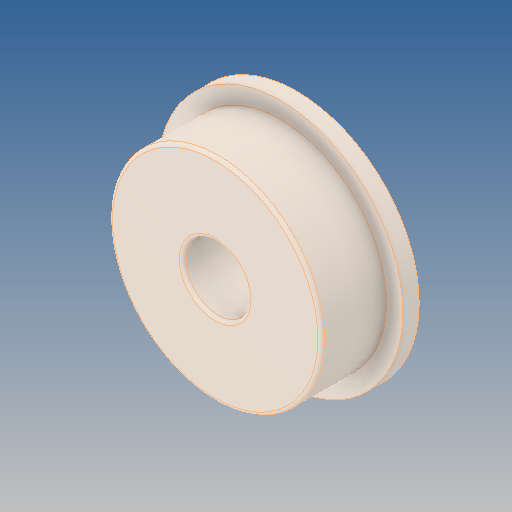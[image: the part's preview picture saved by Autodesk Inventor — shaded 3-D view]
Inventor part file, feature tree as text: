
AUTODESK INVENTOR PART (.ipt)
format: ipt  version: 2019 (Build 230136000, 136)  size: 140,288 bytes
history: native  units: mm
features: fillet x1
ambient origin geometry x8: Origin, YZ Plane, XZ Plane, XY Plane, X Axis, Y Axis, Z Axis, Center Point
bodies: Solid1 (feature_tree)
feature tree (1):
  fillet  "Fillet1"  [1 undecoded]
note: 1 required parameter value undecoded (feature->parameter linkage not recoverable at this tier; creation-order binding heuristic only, values carry confidence <= 0.55)
